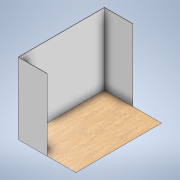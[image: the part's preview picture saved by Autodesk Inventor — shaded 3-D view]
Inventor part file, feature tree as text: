
AUTODESK INVENTOR PART (.ipt)
format: ipt  version: 2020 (Build 240168000, 168)  size: 142,848 bytes
history: native  units: in
note: dims shown in document units (in); Inventor stores cm internally (conversion verified against a paired STEP export)
features: extrude x2, sketch x2
ambient origin geometry x8: Origin, YZ Plane, XZ Plane, XY Plane, X Axis, Y Axis, Z Axis, Center Point
bodies: Body1 (feature_tree)
feature tree (4):
  extrude  "Extrusion2"  Depth=118.1102in
  extrude  "Extrusion3"  Depth=0.3937in
  sketch  "Sketch1"  dims[d2=78.7402in d3=118.1102in]
  sketch  "Sketch3"  dims[d4=0.0394in d5=0.0in d6=0.3937in d7=0.3937in d8=39.3701in d9=39.3701in d10=0.3937in d11=98.4252in d12=0.0in]
